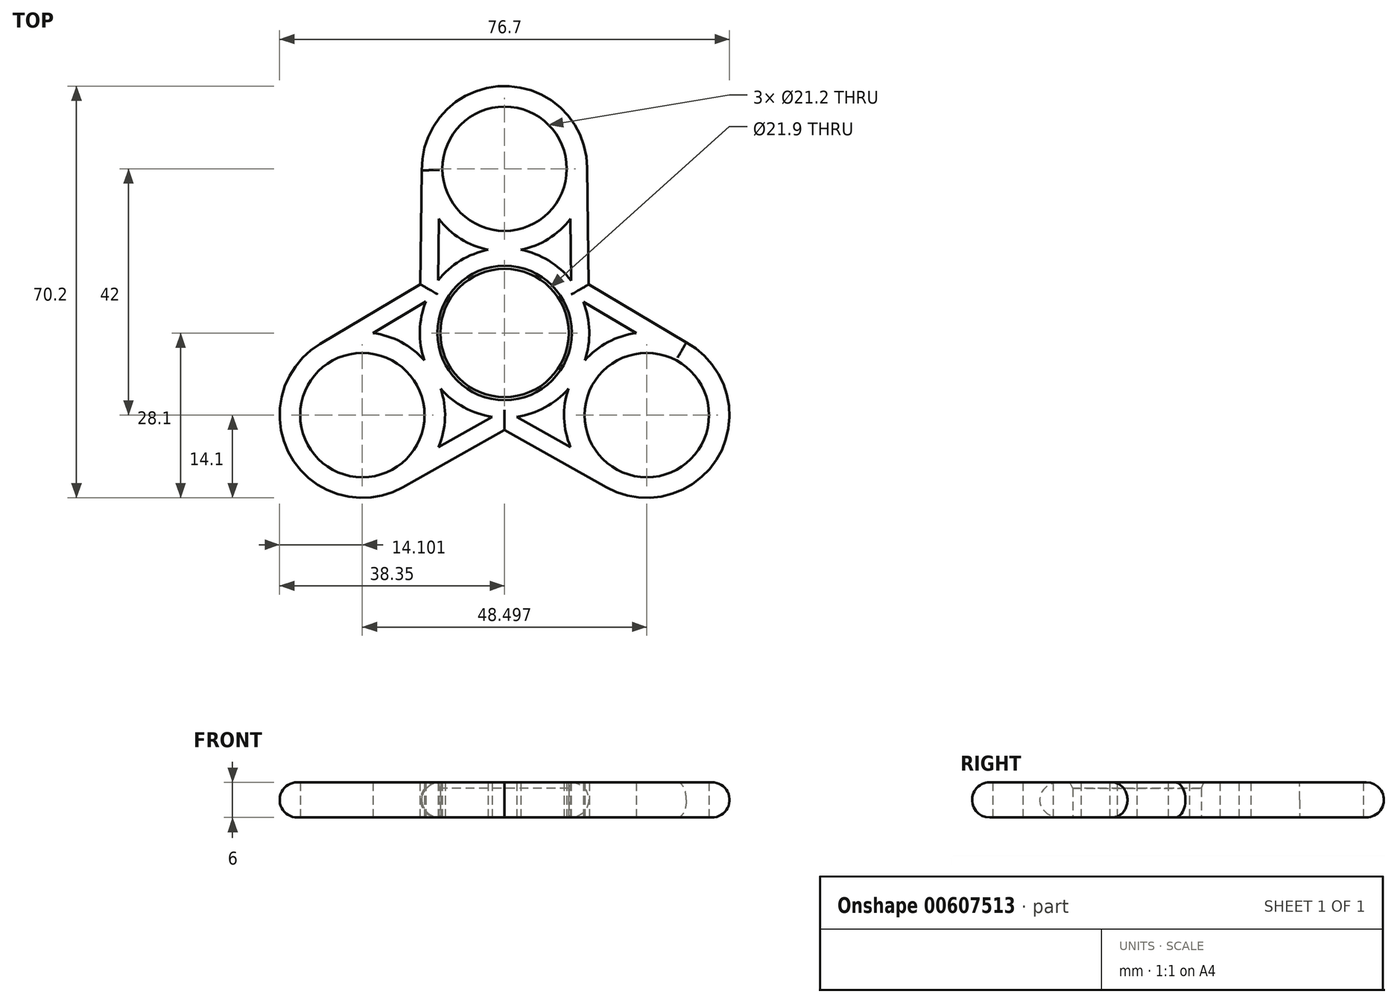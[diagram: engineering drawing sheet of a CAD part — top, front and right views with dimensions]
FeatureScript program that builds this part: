
annotation { "Feature Type Name" : "Feature", "Feature Type Description" : "" }
export const myFeature = defineFeature(function(context is Context, id is Id, definition is map)
    precondition{}
    {
        {
            var Q0;
            Q0=qCreatedBy(makeId("Top.planeOp"),FACE);
            var sketch = newSketch(context, id + "F0", { "sketchPlane" : qUnion([Q0])});
            skCircle(sketch, "E0", {"center": v(0, 0) * mm, "radius": 10.95 * mm});
            skCircle(sketch, "E1.0", {"center": v(0, 0) * mm, "radius": 14.45 * mm});
            skCircle(sketch, "E2.cCircle", {"center": v(0, 0) * mm, "radius": 14 * mm, "construction": true});
            skLineSegment(sketch, "E2.0", {"start": v(-24.25, -14) * mm, "end": v(0, 28) * mm, "construction": true});
            skLineSegment(sketch, "E2.1", {"start": v(0, 28) * mm, "end": v(24.25, -14) * mm, "construction": true});
            skLineSegment(sketch, "E2.2", {"start": v(24.25, -14) * mm, "end": v(-24.25, -14) * mm, "construction": true});
            skPoint(sketch, "E2.0.midPoint", {"position": v(-12.12, 7) * mm});
            skCircle(sketch, "E3", {"center": v(0, 28) * mm, "radius": 10.6 * mm});
            skCircle(sketch, "E4.0", {"center": v(0, 28) * mm, "radius": 14.1 * mm});
            skCircle(sketch, "E5", {"center": v(24.25, -14) * mm, "radius": 10.6 * mm});
            skCircle(sketch, "E6.0", {"center": v(24.25, -14) * mm, "radius": 14.1 * mm});
            skCircle(sketch, "E7", {"center": v(-24.25, -14) * mm, "radius": 10.6 * mm});
            skCircle(sketch, "E8.0", {"center": v(-24.25, -14) * mm, "radius": 14.1 * mm});
            skLineSegment(sketch, "E9", {"start": v(14.1, 28.18) * mm, "end": v(14.45, 0) * mm});
            skLineSegment(sketch, "E10", {"start": v(-14.1, 27.75) * mm, "end": v(-14.45, 0) * mm});
            skLineSegment(sketch, "E11.0", {"start": v(-11.1, 27.71) * mm, "end": v(-11.45, -0.04) * mm});
            skLineSegment(sketch, "E12.0", {"start": v(11.1, 28.14) * mm, "end": v(11.45, -0.04) * mm});
            skLineSegment(sketch, "E13", {"start": v(-31.45, -1.88) * mm, "end": v(-7.38, 12.42) * mm});
            skLineSegment(sketch, "E14", {"start": v(-17.35, -26.3) * mm, "end": v(7.07, -12.6) * mm});
            skLineSegment(sketch, "E15.0", {"start": v(-18.82, -23.68) * mm, "end": v(5.6, -9.99) * mm});
            skLineSegment(sketch, "E16.0", {"start": v(-29.92, -4.46) * mm, "end": v(-5.85, 9.84) * mm});
            skLineSegment(sketch, "E17", {"start": v(17.35, -26.3) * mm, "end": v(-7.07, -12.6) * mm});
            skLineSegment(sketch, "E18", {"start": v(30.97, -1.6) * mm, "end": v(7.39, 12.42) * mm});
            skLineSegment(sketch, "E19.0", {"start": v(29.44, -4.19) * mm, "end": v(5.85, 9.84) * mm});
            skLineSegment(sketch, "E20.0", {"start": v(18.82, -23.68) * mm, "end": v(-5.6, -9.99) * mm});
            skSolve(sketch);
        }
        {
            var Q0;
            Q0 = qSketchRegion(id + "F0", true);
            var Q1;
            Q1=makeQuery(id+"F0.imprint","IMPRINT",FACE,{"disambiguationData":[TD([[makeQuery(id+"F0.imprint","IMPRINT",EDGE,{"derivedFrom":sQuery(id+"F0.wireOp",EDGE,"E0")}),-1.0]])]});
            var Q2;
            {var subQ0=sQuery(id+"F0.wireOp",EDGE,"E11.0");var subQ1=sQuery(id+"F0.wireOp",EDGE,"E1.0");var subQ2=makeQuery(id+"F0.imprint","INTERSECT",VERTEX,{"derivedFrom":[subQ1,subQ0]});Q2=makeQuery(id+"F0.imprint","IMPRINT",FACE,{"disambiguationData":[TD([[makeQuery(id+"F0.imprint","IMPRINT",EDGE,{"disambiguationData":[TD([[subQ2,-1.0]])],"derivedFrom":subQ1}),1.0]])]});}
            var Q3;
            {var subQ0=sQuery(id+"F0.wireOp",EDGE,"E15.0");var subQ1=sQuery(id+"F0.wireOp",EDGE,"E1.0");var subQ2=makeQuery(id+"F0.imprint","INTERSECT",VERTEX,{"derivedFrom":[subQ1,subQ0]});Q3=makeQuery(id+"F0.imprint","IMPRINT",FACE,{"disambiguationData":[TD([[makeQuery(id+"F0.imprint","IMPRINT",EDGE,{"disambiguationData":[TD([[subQ2,-1.0]])],"derivedFrom":subQ1}),1.0]])]});}
            var Q4;
            {var subQ0=sQuery(id+"F0.wireOp",EDGE,"E19.0");var subQ1=sQuery(id+"F0.wireOp",EDGE,"E1.0");var subQ2=makeQuery(id+"F0.imprint","INTERSECT",VERTEX,{"derivedFrom":[subQ1,subQ0]});Q4=makeQuery(id+"F0.imprint","IMPRINT",FACE,{"disambiguationData":[TD([[makeQuery(id+"F0.imprint","IMPRINT",EDGE,{"disambiguationData":[TD([[subQ2,-1.0]])],"derivedFrom":subQ1}),1.0]])]});}
            var Q5;
            {var subQ0=sQuery(id+"F0.wireOp",EDGE,"E6.0");var subQ1=sQuery(id+"F0.wireOp",EDGE,"E1.0");var subQ2=makeQuery(id+"F0.imprint","INTERSECT",VERTEX,{"disambiguationData":[OD(0.0)],"derivedFrom":[subQ1,subQ0]});Q5=makeQuery(id+"F0.imprint","IMPRINT",FACE,{"disambiguationData":[TD([[makeQuery(id+"F0.imprint","IMPRINT",EDGE,{"disambiguationData":[TD([[subQ2,-1.0]])],"derivedFrom":subQ1}),1.0]])]});}
            var Q6;
            {var subQ0=sQuery(id+"F0.wireOp",EDGE,"E4.0");var subQ1=sQuery(id+"F0.wireOp",EDGE,"E1.0");var subQ2=makeQuery(id+"F0.imprint","INTERSECT",VERTEX,{"disambiguationData":[OD(0.0)],"derivedFrom":[subQ1,subQ0]});Q6=makeQuery(id+"F0.imprint","IMPRINT",FACE,{"disambiguationData":[TD([[makeQuery(id+"F0.imprint","IMPRINT",EDGE,{"disambiguationData":[TD([[subQ2,-1.0]])],"derivedFrom":subQ1}),1.0]])]});}
            var Q7;
            {var subQ0=sQuery(id+"F0.wireOp",EDGE,"E8.0");var subQ1=sQuery(id+"F0.wireOp",EDGE,"E1.0");var subQ2=makeQuery(id+"F0.imprint","INTERSECT",VERTEX,{"disambiguationData":[OD(0.0)],"derivedFrom":[subQ1,subQ0]});Q7=makeQuery(id+"F0.imprint","IMPRINT",FACE,{"disambiguationData":[TD([[makeQuery(id+"F0.imprint","IMPRINT",EDGE,{"disambiguationData":[TD([[subQ2,-1.0]])],"derivedFrom":subQ1}),1.0]])]});}
            extrude(context, id + "F1", {"entities" : qUnion([Q0, Q1, Q2, Q3, Q4, Q5, Q6, Q7]), "depth" : 6 * mm, "offsetDistance" : 25 * mm});
        }
        {
            var Q0;
            {var subQ0=sQuery(id+"F0.wireOp",EDGE,"E8.0");Q0=makeQuery(id+"F1.opExtrude","CAP_EDGE",EDGE,{"disambiguationData":[OSD([subQ0]),TDD([makeQuery(id+"F0.imprint","IMPRINT",EDGE,{"disambiguationData":[TD([[makeQuery(id+"F0.imprint","INTERSECT",VERTEX,{"derivedFrom":[subQ0,sQuery(id+"F0.wireOp",EDGE,"E13")]}),-1.0]])],"derivedFrom":subQ0})])],"isStart":false});}
            var Q1;
            Q1=makeQuery(id+"F1.opExtrude","CAP_EDGE",EDGE,{"disambiguationData":[OSD([sQuery(id+"F0.wireOp",EDGE,"E17")])],"isStart":false});
            var Q2;
            Q2=makeQuery(id+"F1.opExtrude","CAP_EDGE",EDGE,{"disambiguationData":[OSD([sQuery(id+"F0.wireOp",EDGE,"E9")])],"isStart":false});
            var Q3;
            Q3=makeQuery(id+"F1.opExtrude","CAP_EDGE",EDGE,{"disambiguationData":[OSD([sQuery(id+"F0.wireOp",EDGE,"E17")])],"isStart":true});
            var Q4;
            Q4=makeQuery(id+"F1.opExtrude","CAP_EDGE",EDGE,{"disambiguationData":[OSD([sQuery(id+"F0.wireOp",EDGE,"E9")])],"isStart":true});
            var Q5;
            Q5=makeQuery(id+"F1.opExtrude","CAP_EDGE",EDGE,{"disambiguationData":[OSD([sQuery(id+"F0.wireOp",EDGE,"E13")])],"isStart":true});
            fillet(context, id + "F2", {"entities" : qUnion([Q0, Q1, Q2, Q3, Q4, Q5]), "radius" : 3 * mm, "tangentPropagation" : true, "allowEdgeOverflow" : false});
        }
        {
            var Q0;
            Q0=makeQuery(id+"F1.opExtrude","CAP_EDGE",EDGE,{"disambiguationData":[OSD([sQuery(id+"F0.wireOp",EDGE,"E0")])],"isStart":false});
            chamfer(context, id + "F3", {"entities" : qUnion([Q0]), "chamferType" : ChamferType.TWO_OFFSETS, "width1" : 1 * mm, "oppositeDirection" : false, "width2" : .5 * mm, "tangentPropagation" : true});
        }
    });
